# Revit family: HVAC_Fireplaces_Regency-Fireplace_Grandview-gas-fireplace_G800EC
name_source: partatom
category: Specialty Equipment
units: mm (PartAtom-declared; Revit-internal decimal feet)

## family parameters
Classification Number = 23.40.20.34.14
Cut with Voids When Loaded = No
Enable Cutting in Views = No
Host = Face
Maintain Annotation Orientation = No
Part Type = Normal
Room Calculation Point = No
Round Connector Dimension = Use Diameter
Shared = No

## types (2) — shared parameters
Apparent Load = 0 VA
Clean Front - Cool wall Installation = Clean Front - Cool wall Installation
Clean Front - Non-Combustible Installation = Clean Front - Non-Combustible Installation
Current = 2 A
Depth = 17 "
Description = Choose stunning flame picture, choose your accessories, and create a one-of-a-kind fireplace. The Regency Grandview G800EC is the first of our Grandview series of gas fireplaces that are designed to maximize choice and customization.
Duct Connector Description = 4” Inner / 6-5/8” Outer
Duct Diameter = 7 "
Frequency = 60 Hz
Gas flow = 0.0 L/s
Height = 34 "
Housing Material = Regency Fireplace - Metal - Black
Manufacturer = Regency Fireplace
Maximum Supply Pressure = 14” W.C. (3.48 kPa)
Number of Poles = 1
Outside Finish w-Faceplate - Non-Combustible Installation = Outside Finish w-Faceplate - Non-Combustible Installation
Outside Finish w-Finishing Trim - Cool wall Installation = Outside Finish w-Finishing Trim - Cool wall Installation
Pipe Diameter = 1 "
Power Consumption = 0 W
Power Factor = 1
Product Documentation Link = https://assets.regency-fire.com
Product Page URL = https://www.regency-fire.com
Product data url = https://www.bimobject.com
URL = https://www.regency-fire.com
Ventilation flow = 100.0 CFM
Voltage = 120 V
Width = 36 "
zero-valued in all types: Default Elevation, Version

## per-type parameters (varying)
| type | CSA P.4.1 | Fuel Type | Gas Connector Description | Manifold Pressure - High | Manifold Pressure - Low | Maximum Input Altitude 0-4500 ft. (0-1372m) | Minimum Input Altitude 0-4500 ft. (0-1372m) | Minimum Supply Pressure | Orifce Size -Altitude 0-4500 ft |
| G800EC-NG | 55.96% | Natural Gas | Natural gas supply | 3.8” W.C. (0.94 kPa) | 1.1” W.C. (0.27 kPa) | 27,000 Btu/h (7.91 kW) | 15,000 Btu/h (4.4kW) | 5” W.C. (1.25 kPa) | # 42 DMS |
| G800EC-LP | 57.74% | Propane | Propane gas supply | 10” W.C. (2.49 kPa) | 6.4” W.C. (1.60 kPa) | 25,500 Btu/h (7.47 kW) | 21,000 Btu/h (6.15 kW) | 11” W.C. (2.74 kPa) | # 53 DMS |

note: column(s) folded — value = type name in every type: Model

## geometry (parser evidence)
native form markers: Sweep x15
no freeform markers — native parametric forms only
